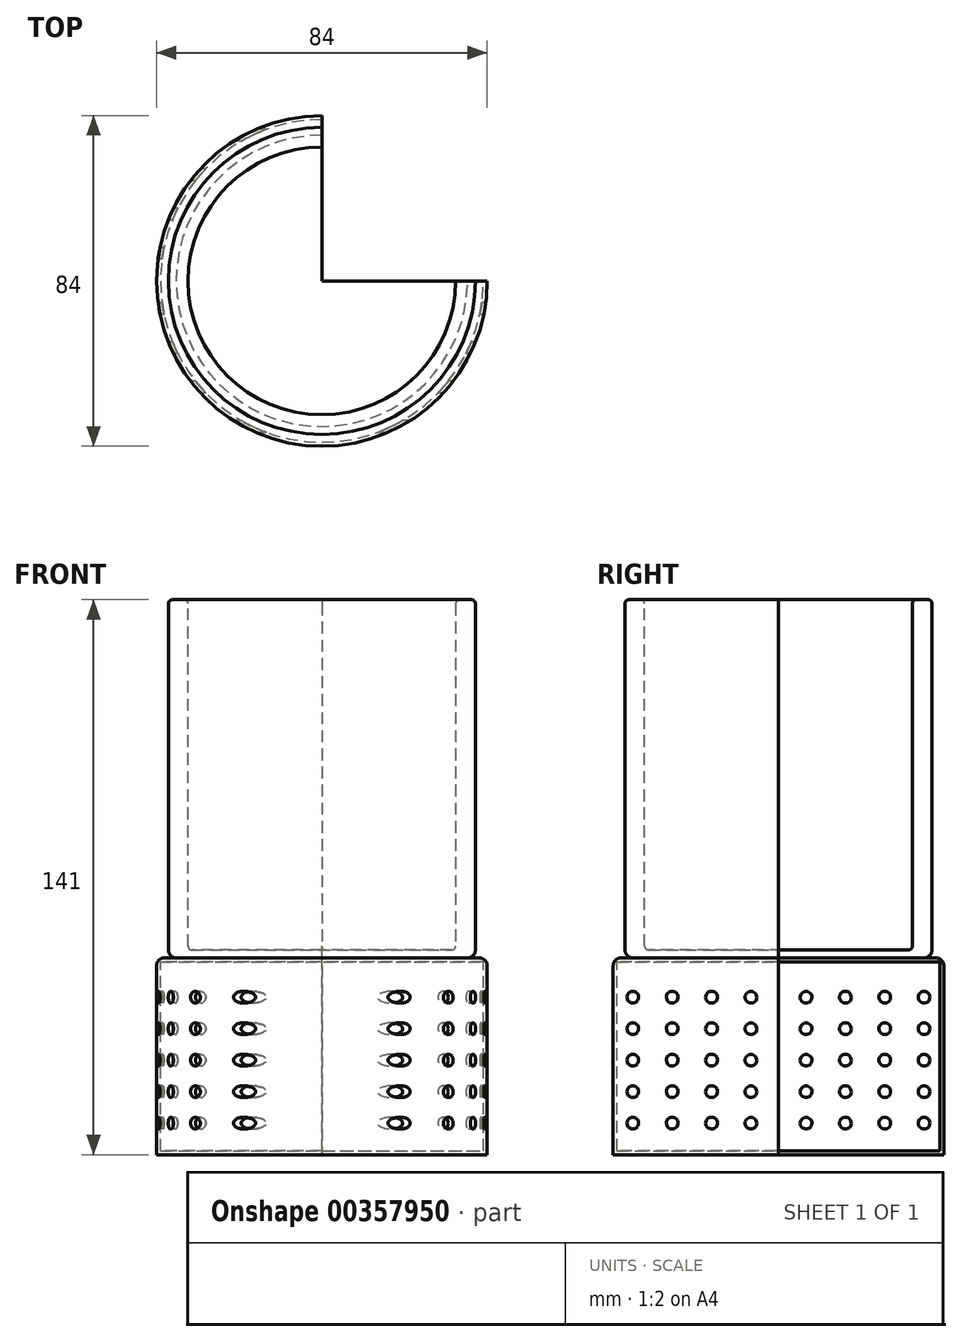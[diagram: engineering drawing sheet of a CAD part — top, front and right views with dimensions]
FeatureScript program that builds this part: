
annotation { "Feature Type Name" : "Feature", "Feature Type Description" : "" }
export const myFeature = defineFeature(function(context is Context, id is Id, definition is map)
    precondition{}
    {
        {
            var Q0;
            Q0=qCreatedBy(makeId("Front.planeOp"),FACE);
            var sketch = newSketch(context, id + "F0", { "sketchPlane" : qUnion([Q0])});
            skLineSegment(sketch, "E0", {"start": v(0, 161.65) * mm, "end": v(0, -240.28) * mm, "construction": true});
            skLineSegment(sketch, "E1", {"start": v(38, 89) * mm, "end": v(35, 89) * mm});
            skLineSegment(sketch, "E2", {"start": v(34, 88) * mm, "end": v(34, 1) * mm});
            skLineSegment(sketch, "E3", {"start": v(33, 0) * mm, "end": v(0, 0) * mm});
            skLineSegment(sketch, "E4", {"start": v(39, 88) * mm, "end": v(39, 0) * mm});
            skLineSegment(sketch, "E5", {"start": v(0, -2) * mm, "end": v(0, 0) * mm});
            skPoint(sketch, "E6.visualSharp", {"position": v(39, 89) * mm});
            skArc(sketch, "E6.filletArc", {"start": v(39, 88) * mm, "mid": v(38.7, 88.7) * mm, "end": v(38, 89) * mm});
            skPoint(sketch, "E7.visualSharp", {"position": v(34, 89) * mm});
            skArc(sketch, "E7.filletArc", {"start": v(35, 89) * mm, "mid": v(34.3, 88.7) * mm, "end": v(34, 88) * mm});
            skPoint(sketch, "E8.visualSharp", {"position": v(34, 0) * mm});
            skArc(sketch, "E8.filletArc", {"start": v(33, 0) * mm, "mid": v(33.7, 0.3) * mm, "end": v(34, 1) * mm});
            skLineSegment(sketch, "E9", {"start": v(0, -2) * mm, "end": v(37, -2) * mm});
            skPoint(sketch, "E10.visualSharp", {"position": v(39, -2) * mm});
            skArc(sketch, "E10.filletArc", {"start": v(37, -2) * mm, "mid": v(38.41, -1.41) * mm, "end": v(39, 0) * mm});
            skSolve(sketch);
        }
        {
            var Q0;
            Q0=qSketchRegion(id+"F0",true);
            var Q1;
            Q1=sQuery(id+"F0.wireOp",EDGE,"E0");
            revolve(context, id + "F1", {"entities" : qUnion([Q0]), "axis" : qUnion([Q1]), "revolveType" : RevolveType.ONE_DIRECTION, "angle" : 270 * degree});
        }
        {
            var Q0;
            Q0=qCreatedBy(makeId("Front.planeOp"),FACE);
            var sketch = newSketch(context, id + "F2", { "sketchPlane" : qUnion([Q0])});
            skLineSegment(sketch, "E11.0", {"start": v(-37, -2) * mm, "end": v(37, -2) * mm, "construction": true});
            skLineSegment(sketch, "E12", {"start": v(42, -2) * mm, "end": v(0, -2) * mm});
            skLineSegment(sketch, "E13", {"start": v(42, -2) * mm, "end": v(42, -52) * mm});
            skLineSegment(sketch, "E14", {"start": v(42, -52) * mm, "end": v(0, -52) * mm});
            skLineSegment(sketch, "E15", {"start": v(0, -52) * mm, "end": v(0, -51) * mm});
            skLineSegment(sketch, "E16", {"start": v(0, -51) * mm, "end": v(41, -51) * mm});
            skLineSegment(sketch, "E17", {"start": v(41, -51) * mm, "end": v(41, -3) * mm});
            skLineSegment(sketch, "E18", {"start": v(41, -3) * mm, "end": v(0, -3) * mm});
            skLineSegment(sketch, "E19", {"start": v(0, -3) * mm, "end": v(0, -2) * mm});
            skLineSegment(sketch, "E20", {"start": v(0, 63.1) * mm, "end": v(0, -71.51) * mm, "construction": true});
            skSolve(sketch);
        }
        {
            var Q0;
            Q0 = qSketchRegion(id + "F2", true);
            var Q1;
            Q1=sQuery(id+"F2.wireOp",EDGE,"E20");
            revolve(context, id + "F3", {"operationType" : NewBodyOperationType.ADD, "entities" : qUnion([Q0]), "axis" : qUnion([Q1]), "revolveType" : RevolveType.ONE_DIRECTION, "angle" : 270 * degree});
        }
        {
            var Q0;
            Q0=makeQuery(id+"F3.opRevolve","SWEPT_EDGE",EDGE,{"disambiguationData":[OSD([sQuery(id+"F2.wireOp",EDGE,"E12"),sQuery(id+"F2.wireOp",EDGE,"E13")])]});
            fillet(context, id + "F4", {"entities" : qUnion([Q0]), "radius" : 2 * mm, "tangentPropagation" : true, "allowEdgeOverflow" : false});
        }
        {
            var Q0;
            Q0=qCreatedBy(makeId("Right.planeOp"),FACE);
            var sketch = newSketch(context, id + "F5", { "sketchPlane" : qUnion([Q0])});
            skLineSegment(sketch, "E21", {"start": v(-42, -52) * mm, "end": v(-42, -4) * mm, "construction": true});
            skLineSegment(sketch, "E22.0", {"start": v(42, -4) * mm, "end": v(42, -52) * mm, "construction": true});
            skLineSegment(sketch, "E23.0", {"start": v(42, -52) * mm, "end": v(0, -52) * mm, "construction": true});
            skCircle(sketch, "E24", {"center": v(-37, -12) * mm, "radius": 1.5 * mm});
            skCircle(sketch, "E25", {"center": v(-27, -12) * mm, "radius": 1.5 * mm});
            skCircle(sketch, "E26", {"center": v(-17, -12) * mm, "radius": 1.5 * mm});
            skCircle(sketch, "E27", {"center": v(-7, -12) * mm, "radius": 1.5 * mm});
            skCircle(sketch, "E28", {"center": v(-37, -20) * mm, "radius": 1.5 * mm});
            skCircle(sketch, "E29", {"center": v(-17, -20) * mm, "radius": 1.5 * mm});
            skCircle(sketch, "E30", {"center": v(-7, -20) * mm, "radius": 1.5 * mm});
            skCircle(sketch, "E31", {"center": v(-7, -28) * mm, "radius": 1.5 * mm});
            skCircle(sketch, "E32", {"center": v(-27, -20) * mm, "radius": 1.5 * mm});
            skCircle(sketch, "E33", {"center": v(-37, -28) * mm, "radius": 1.5 * mm});
            skCircle(sketch, "E34", {"center": v(-37, -44) * mm, "radius": 1.5 * mm});
            skCircle(sketch, "E35", {"center": v(-27, -28) * mm, "radius": 1.5 * mm});
            skCircle(sketch, "E36", {"center": v(-37, -36) * mm, "radius": 1.5 * mm});
            skCircle(sketch, "E37", {"center": v(-27, -44) * mm, "radius": 1.5 * mm});
            skCircle(sketch, "E38", {"center": v(-17, -28) * mm, "radius": 1.5 * mm});
            skCircle(sketch, "E39", {"center": v(-17, -44) * mm, "radius": 1.5 * mm});
            skCircle(sketch, "E40", {"center": v(-17, -36) * mm, "radius": 1.5 * mm});
            skCircle(sketch, "E41", {"center": v(-7, -36) * mm, "radius": 1.5 * mm});
            skCircle(sketch, "E42", {"center": v(-27, -36) * mm, "radius": 1.5 * mm});
            skLineSegment(sketch, "E43", {"start": v(-42, -12) * mm, "end": v(0, -12) * mm, "construction": true});
            skLineSegment(sketch, "E44", {"start": v(-42, -20) * mm, "end": v(0, -20) * mm, "construction": true});
            skLineSegment(sketch, "E45", {"start": v(0, -28) * mm, "end": v(-42, -28) * mm, "construction": true});
            skLineSegment(sketch, "E46", {"start": v(0, -36) * mm, "end": v(-42, -36) * mm, "construction": true});
            skLineSegment(sketch, "E47", {"start": v(0, -44) * mm, "end": v(-42, -44) * mm, "construction": true});
            skCircle(sketch, "E48", {"center": v(-7, -44) * mm, "radius": 1.5 * mm});
            skLineSegment(sketch, "E49", {"start": v(-37, -3.78) * mm, "end": v(-37, -52.1) * mm, "construction": true});
            skLineSegment(sketch, "E50", {"start": v(-27, -3.54) * mm, "end": v(-27, -53.55) * mm, "construction": true});
            skLineSegment(sketch, "E51", {"start": v(-17, -3.78) * mm, "end": v(-17, -52.78) * mm, "construction": true});
            skLineSegment(sketch, "E52", {"start": v(-7, -3.61) * mm, "end": v(-7, -52.94) * mm, "construction": true});
            skCircle(sketch, "E53.MirrorC", {"center": v(17, -28) * mm, "radius": 1.5 * mm});
            skCircle(sketch, "E54.MirrorC", {"center": v(7, -28) * mm, "radius": 1.5 * mm});
            skCircle(sketch, "E55.MirrorC", {"center": v(17, -12) * mm, "radius": 1.5 * mm});
            skCircle(sketch, "E56.MirrorC", {"center": v(37, -12) * mm, "radius": 1.5 * mm});
            skCircle(sketch, "E57.MirrorC", {"center": v(7, -12) * mm, "radius": 1.5 * mm});
            skCircle(sketch, "E58.MirrorC", {"center": v(27, -44) * mm, "radius": 1.5 * mm});
            skCircle(sketch, "E59.MirrorC", {"center": v(37, -20) * mm, "radius": 1.5 * mm});
            skCircle(sketch, "E60.MirrorC", {"center": v(17, -20) * mm, "radius": 1.5 * mm});
            skCircle(sketch, "E61.MirrorC", {"center": v(27, -36) * mm, "radius": 1.5 * mm});
            skCircle(sketch, "E62.MirrorC", {"center": v(27, -12) * mm, "radius": 1.5 * mm});
            skCircle(sketch, "E63.MirrorC", {"center": v(27, -20) * mm, "radius": 1.5 * mm});
            skCircle(sketch, "E64.MirrorC", {"center": v(37, -36) * mm, "radius": 1.5 * mm});
            skCircle(sketch, "E65.MirrorC", {"center": v(17, -36) * mm, "radius": 1.5 * mm});
            skCircle(sketch, "E66.MirrorC", {"center": v(7, -36) * mm, "radius": 1.5 * mm});
            skCircle(sketch, "E67.MirrorC", {"center": v(27, -28) * mm, "radius": 1.5 * mm});
            skCircle(sketch, "E68.MirrorC", {"center": v(37, -28) * mm, "radius": 1.5 * mm});
            skCircle(sketch, "E69.MirrorC", {"center": v(37, -44) * mm, "radius": 1.5 * mm});
            skCircle(sketch, "E70.MirrorC", {"center": v(17, -44) * mm, "radius": 1.5 * mm});
            skCircle(sketch, "E71.MirrorC", {"center": v(7, -20) * mm, "radius": 1.5 * mm});
            skCircle(sketch, "E72.MirrorC", {"center": v(7, -44) * mm, "radius": 1.5 * mm});
            skSolve(sketch);
        }
        {
            var Q0;
            Q0 = qSketchRegion(id + "F5", true);
            extrude(context, id + "F6", {"entities" : qUnion([Q0]), "operationType" : NewBodyOperationType.REMOVE, "endBound" : BoundingType.THROUGH_ALL, "depth" : 25 * mm, "hasSecondDirection" : true, "secondDirectionBound" : SecondDirectionBoundingType.THROUGH_ALL, "secondDirectionOppositeDirection" : true, "secondDirectionDepth" : 25 * mm});
        }
    });
